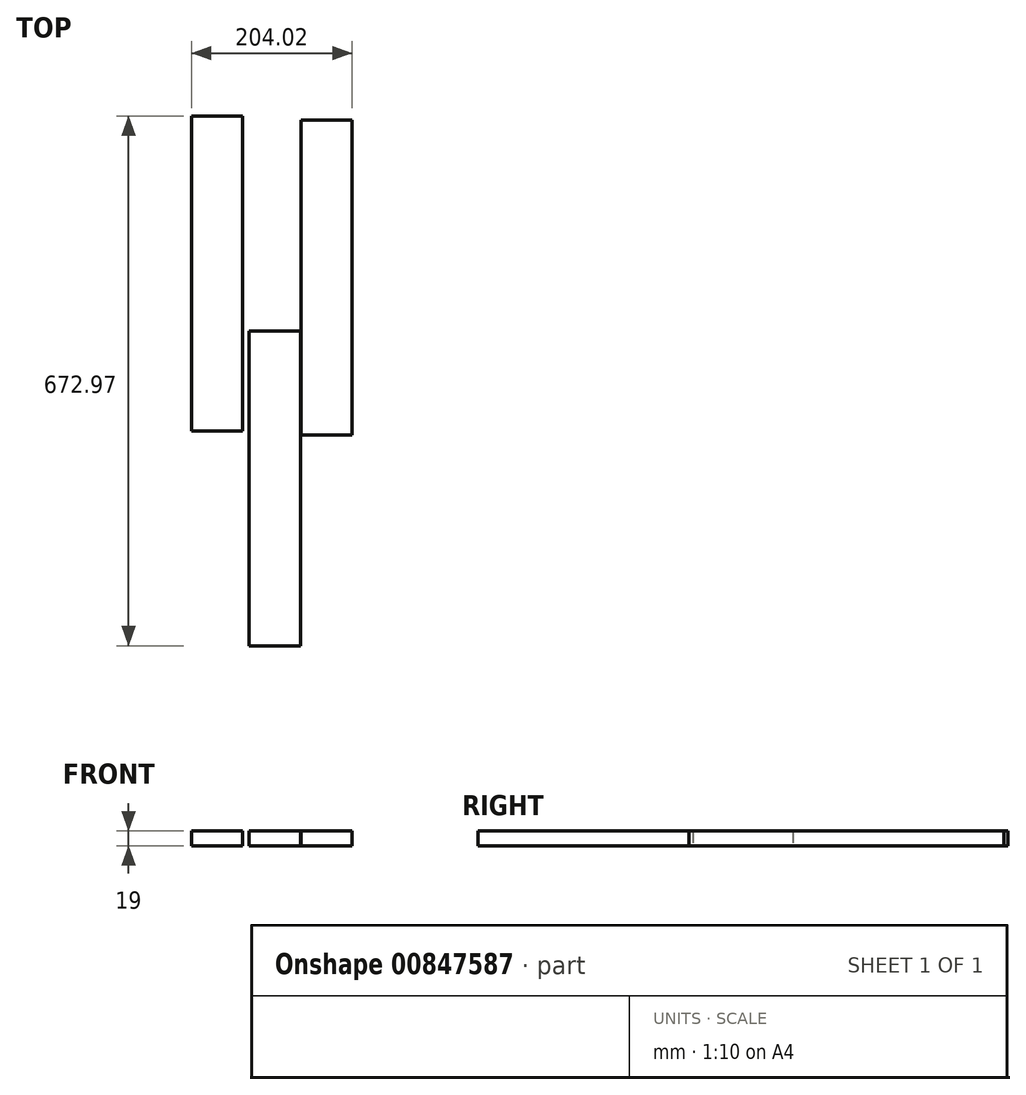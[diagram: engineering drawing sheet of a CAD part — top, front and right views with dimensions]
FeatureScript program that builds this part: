
annotation { "Feature Type Name" : "Feature", "Feature Type Description" : "" }
export const myFeature = defineFeature(function(context is Context, id is Id, definition is map)
    precondition{}
    {
        {
            var Q0;
            Q0=qCreatedBy(makeId("Top.planeOp"),FACE);
            var sketch = newSketch(context, id + "F0", { "sketchPlane" : qUnion([Q0])});
            skLineSegment(sketch, "E0.bottom", {"start": v(9.4, 162.03) * mm, "end": v(-55.6, 162.03) * mm});
            skLineSegment(sketch, "E0.top", {"start": v(9.4, -237.97) * mm, "end": v(-55.6, -237.97) * mm});
            skLineSegment(sketch, "E0.left", {"start": v(9.4, 162.03) * mm, "end": v(9.4, -237.97) * mm});
            skLineSegment(sketch, "E0.right", {"start": v(-55.6, 162.03) * mm, "end": v(-55.6, -237.97) * mm});
            skSolve(sketch);
        }
        {
            var Q0;
            Q0=makeQuery(id+"F0.imprint","IMPRINT",FACE,{"disambiguationData":[TD([[makeQuery(id+"F0.imprint","IMPRINT",EDGE,{"derivedFrom":sQuery(id+"F0.wireOp",EDGE,"E0.bottom")}),1.0]])]});
            var sketch = newSketch(context, id + "F1", { "sketchPlane" : qUnion([Q0])});
            skSolve(sketch);
        }
        {
            var Q0;
            Q0 = qSketchRegion(id + "F1", true);
            var Q1;
            Q1=makeQuery(id+"F1.imprint","IMPRINT",FACE,{"disambiguationData":[TD([[makeQuery(id+"F1.imprint","IMPRINT",EDGE,{"derivedFrom":makeQuery(id+"F0.imprint","IMPRINT",EDGE,{"derivedFrom":sQuery(id+"F0.wireOp",EDGE,"E0.bottom")})}),1.0]])]});
            extrude(context, id + "F2", {"entities" : qUnion([Q0, Q1]), "depth" : 19 * mm, "offsetDistance" : 25.4 * mm});
        }
        {
            var Q0;
            Q0=qCreatedBy(makeId("Top.planeOp"),FACE);
            var sketch = newSketch(context, id + "F3", { "sketchPlane" : qUnion([Q0])});
            skLineSegment(sketch, "E1.bottom", {"start": v(-56.24, -506.03) * mm, "end": v(-121.24, -506.03) * mm});
            skLineSegment(sketch, "E1.top", {"start": v(-56.24, -106.03) * mm, "end": v(-121.24, -106.03) * mm});
            skLineSegment(sketch, "E1.left", {"start": v(-56.24, -506.03) * mm, "end": v(-56.24, -106.03) * mm});
            skLineSegment(sketch, "E1.right", {"start": v(-121.24, -506.03) * mm, "end": v(-121.24, -106.03) * mm});
            skSolve(sketch);
        }
        {
            var Q0;
            Q0 = qSketchRegion(id + "F3", true);
            extrude(context, id + "F4", {"entities" : qUnion([Q0]), "depth" : 19 * mm, "offsetDistance" : 25.4 * mm});
        }
        {
            var Q0;
            Q0=qCreatedBy(makeId("Top.planeOp"),FACE);
            var sketch = newSketch(context, id + "F5", { "sketchPlane" : qUnion([Q0])});
            skLineSegment(sketch, "E2.bottom", {"start": v(-129.62, -233.06) * mm, "end": v(-194.62, -233.06) * mm});
            skLineSegment(sketch, "E2.top", {"start": v(-129.62, 166.94) * mm, "end": v(-194.62, 166.94) * mm});
            skLineSegment(sketch, "E2.left", {"start": v(-129.62, -233.06) * mm, "end": v(-129.62, 166.94) * mm});
            skLineSegment(sketch, "E2.right", {"start": v(-194.62, -233.06) * mm, "end": v(-194.62, 166.94) * mm});
            skSolve(sketch);
        }
        {
            var Q0;
            Q0 = qSketchRegion(id + "F5", true);
            extrude(context, id + "F6", {"entities" : qUnion([Q0]), "depth" : 19 * mm, "offsetDistance" : 25.4 * mm});
        }
    });
